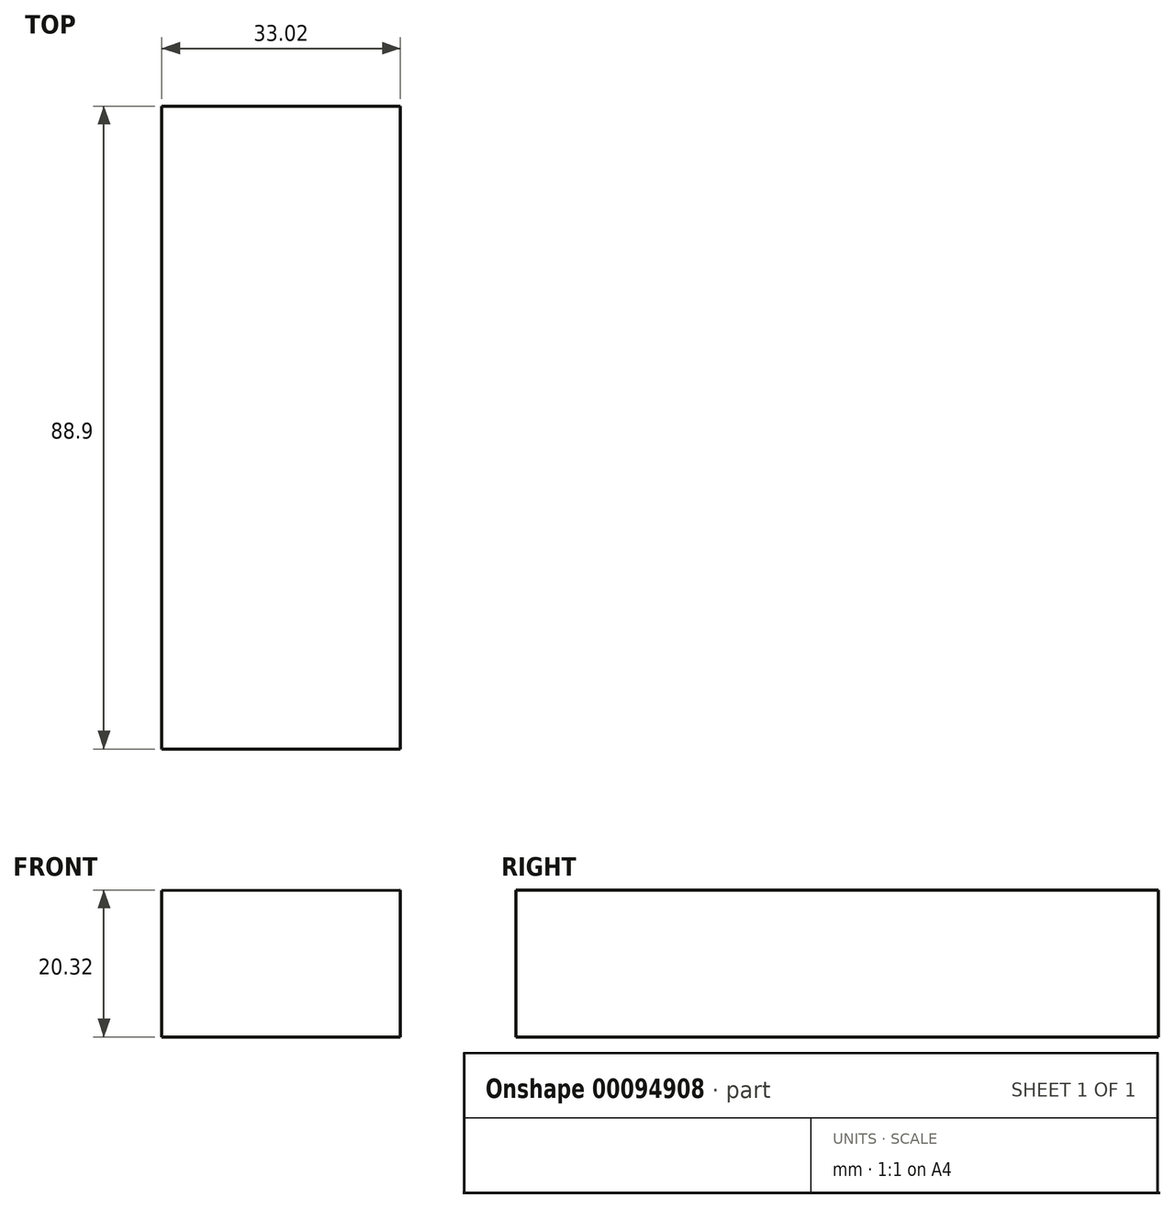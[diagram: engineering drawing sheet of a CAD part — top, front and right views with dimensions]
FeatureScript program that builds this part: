
annotation { "Feature Type Name" : "Feature", "Feature Type Description" : "" }
export const myFeature = defineFeature(function(context is Context, id is Id, definition is map)
    precondition{}
    {
        {
            var Q0;
            Q0=qCreatedBy(makeId("Front.planeOp"),FACE);
            var sketch = newSketch(context, id + "F0", { "sketchPlane" : qUnion([Q0])});
            skLineSegment(sketch, "E0", {"start": v(-11.2, 25.43) * mm, "end": v(-11.2, 5.2) * mm});
            skLineSegment(sketch, "E1", {"start": v(-11.2, 5.2) * mm, "end": v(21.83, 5.2) * mm});
            skLineSegment(sketch, "E2", {"start": v(21.83, 5.2) * mm, "end": v(21.83, 25.53) * mm});
            skLineSegment(sketch, "E3", {"start": v(21.83, 25.53) * mm, "end": v(-11.2, 25.43) * mm});
            skSolve(sketch);
        }
        {
            var Q0;
            Q0 = qSketchRegion(id + "F0", true);
            extrude(context, id + "F1", {"entities" : qUnion([Q0]), "depth" : 88.9 * mm});
        }
    });
